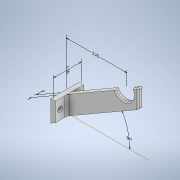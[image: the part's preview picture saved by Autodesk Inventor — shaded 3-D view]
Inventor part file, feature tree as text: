
AUTODESK INVENTOR PART (.ipt)
format: ipt  version: 2021.1 (Build 251245010, 245A)  size: 199,168 bytes
history: native  units: in
note: dims shown in document units (in); Inventor stores cm internally (conversion verified against a paired STEP export)
features: other x5, sketch x4, fillet x4, extrude x3, hole x1
ambient origin geometry x8: Origin, YZ Plane, XZ Plane, XY Plane, X Axis, Y Axis, Z Axis, Center Point
bodies: Solid2 (feature_tree)
feature tree (17):
  other  "Annotations"
  extrude  "Extrusion3"  Depth=0.25in
  extrude  "Extrusion4"  TaperAngle=30.0deg  [1 undecoded]
  sketch  "Sketch7"  dims[d26=1.075in d29=0.25in]
  extrude  "Extrusion5"  Depth=0.25in
  hole  "Hole3"  [1 undecoded]
  fillet  "Fillet3"  [1 undecoded]
  fillet  "Fillet4"  [1 undecoded]
  fillet  "Fillet5"  Radius=0.25in
  fillet  "Fillet6"  Radius=0.25in
  sketch  "Sketch5"  dims[d21=1.0in d22=0.25in]
  sketch  "Sketch6"  dims[d23=1.5in d24=0.0in d25=30.0deg]
  sketch  "Sketch8"  dims[d30=3.25in d31=0.25in d32=0.0in d33=0.0in d34=0.25in d35=0.25in d47=1.5in d48=0.0in d49=0.15in d50=0.75in d51=0.279in d52=0.25in d53=0.5635in d54=1.0in d55=0.8108in d65=0.0625in d66=0.0625in d67=0.0625in d68=0.125in d56=0.2085in d57=0.331in d58=1.5in d59=2.3174in d60=30.0deg d69=3.25in d70=0.3005in d71=0.25in]
  other  "Linear Dimension 1"
  other  "Angular Dimension 1"
  other  "Linear Dimension 2"
  other  "Linear Dimension 3"
note: 4 required parameter values undecoded (feature->parameter linkage not recoverable at this tier; creation-order binding heuristic only, values carry confidence <= 0.55)
